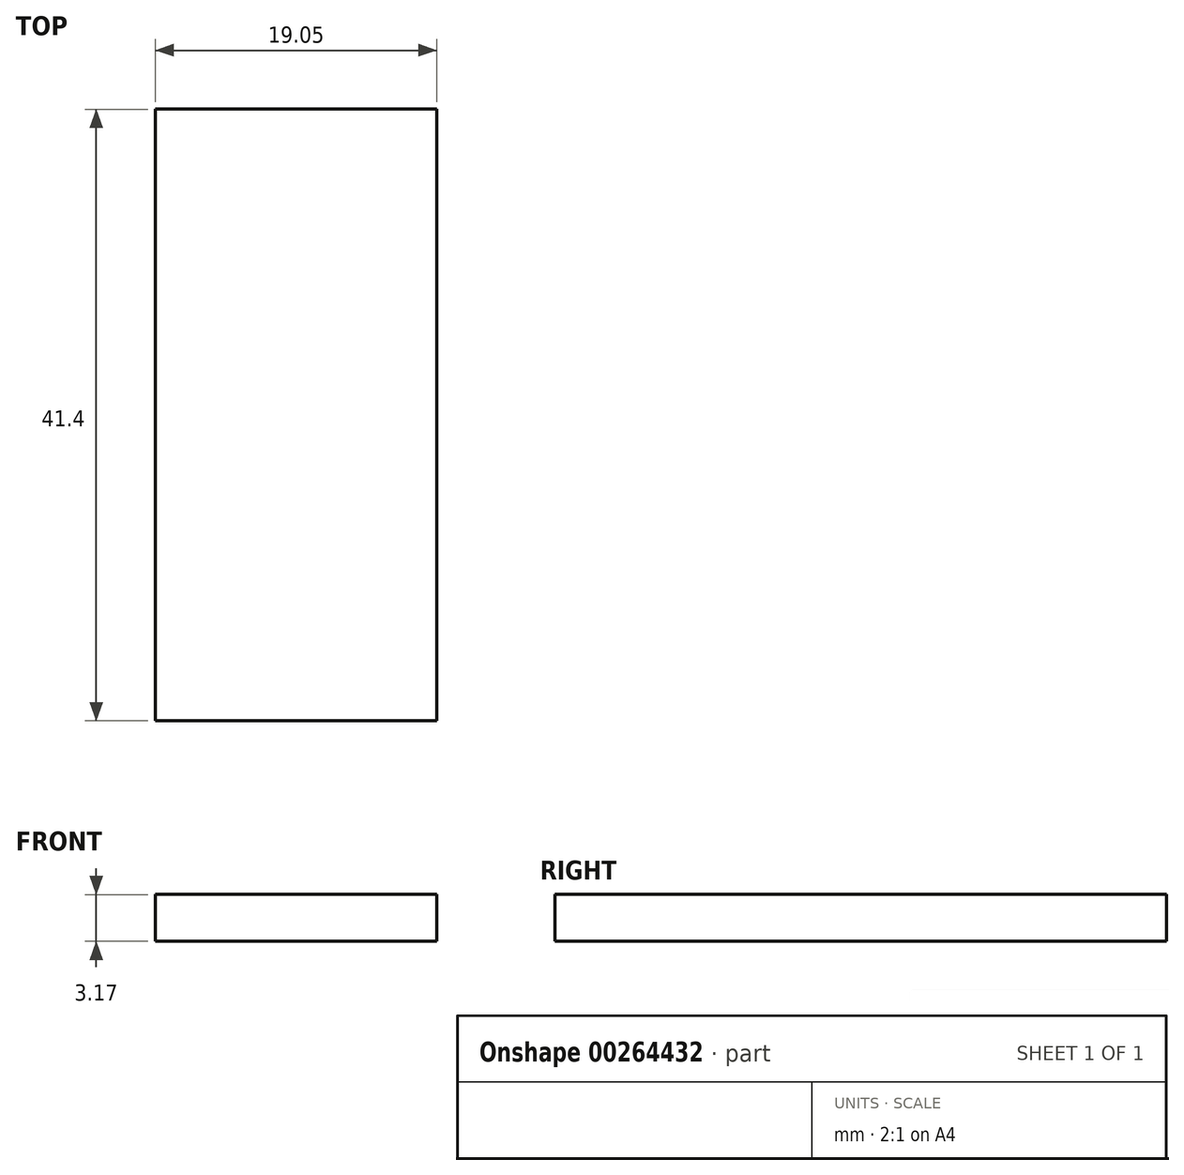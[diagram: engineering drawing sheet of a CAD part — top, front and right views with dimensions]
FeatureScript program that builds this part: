
annotation { "Feature Type Name" : "Feature", "Feature Type Description" : "" }
export const myFeature = defineFeature(function(context is Context, id is Id, definition is map)
    precondition{}
    {
        {
            var Q0;
            Q0=qCreatedBy(makeId("Top.planeOp"),FACE);
            var sketch = newSketch(context, id + "F0", { "sketchPlane" : qUnion([Q0])});
            skLineSegment(sketch, "E0.bottom", {"start": v(7.75, 20.7) * mm, "end": v(-11.3, 20.7) * mm});
            skLineSegment(sketch, "E0.top", {"start": v(7.75, -20.7) * mm, "end": v(-11.3, -20.7) * mm});
            skLineSegment(sketch, "E0.left", {"start": v(7.75, 20.7) * mm, "end": v(7.75, -20.7) * mm});
            skLineSegment(sketch, "E0.right", {"start": v(-11.3, 20.7) * mm, "end": v(-11.3, -20.7) * mm});
            skPoint(sketch, "E0.middle", {"position": v(-1.77, 0) * mm});
            skSolve(sketch);
        }
        {
            var Q0;
            Q0 = qSketchRegion(id + "F0", true);
            extrude(context, id + "F1", {"entities" : qUnion([Q0]), "depth" : 3.17 * mm});
        }
    });
